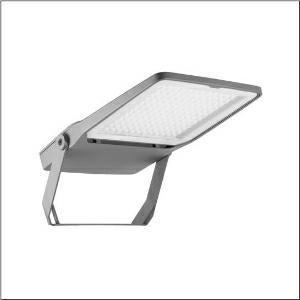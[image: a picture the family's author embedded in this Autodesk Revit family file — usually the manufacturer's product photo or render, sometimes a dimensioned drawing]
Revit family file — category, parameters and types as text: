
# Revit family: floodlight_fl_20_midi___pl52_5xa7681e2d1ac_ecaa
name_source: partatom
category: Lighting Fixtures
units: mm (PartAtom-declared; Revit-internal decimal feet)

## family parameters
Cut with Voids When Loaded = No
Host = Face
Light Source = No
Part Type = Normal
Room Calculation Point = No
Round Connector Dimension = Use Diameter
Shared = No

## types (1)
- Floodlight FL 20 midi  PL52 (1 x LED 4000K / CRI = 70 (unbekannt), 26840 lm, 4000K)
    Apparent Load = 208 VA
    CIE Flux Codes = 27 59 98 100 100
    Color Rendering = 70
    Color Temperature = 4000K
    Default Elevation = 1800 mm
    Description = Floodlight FL 20 midi, floodlight, primary light control with lens, of plastic, primary optical cover: protective disc, of toughened safety glass, transparent, light distribution: PL52, light emission: direct distribution, primary light characteristic: asymmetric, installation type: surface-mounted, LED High Power LED, rated luminous flux: 26.840 lm, light colour: 740, colour temperature: 4000K, control gear: ECG Basic, control: power reduction, overheat protection, electronic power reduction, with terminal, 5-pole, max. 2.5mm², mains connection: 220..240V, AC, 50/60Hz, rated input power: 208W, LED unit, of diecast aluminium, powder-coated, Siteco® metallic grey (DB 702S), length: 654 mm, width: 450 mm, height: 76mm, housing frame, of diecast aluminium, powder-coated, Siteco® metallic grey (DB 702S), mounting bracket, of steel, powder-coated, Siteco® metallic grey (DB 702S), ON/OFFprotection rating (complete): IP66, insulation class (complete): insulation class I (protective earthing), certification: CE, ENEC, VDE, protection symbol: D, permissible ambient temperature for indoor applications: -40..+40°C, permissible ambient temperature for outdoor applications: -40..+50°C, standard: DIN EN 12944, packaging unit: 1 piece

Light Distribution: PL52
    Height = 76 mm
    Lamp = 1 x LED 4000K / CRI >= 70 (unbekannt)
    Lamp Light Flux = 26840 lm
    Lamp count = 1
    Length = 672 mm
    Luminous efficacy = 129 lm/W
    Manufacturer = Siteco
    ModVariant = No
    Model = 5XA7681E2D1AC
    Number of Poles = 1
    OnlyDefault = Yes
    Power Factor = 1
    Product Name = Floodlight FL 20 midi | PL52
    Product group = floodlight | pylon top
    ProductGroupID = 6101
    Protection Class = Protection class I
    Protection Degree = IP 66
    RLX_Detail_Level = 1
    RlxData = <blob elided: 94097 chars, md5=06d9ddb8>
    Socket = socket
    Standby Power = 0 W
    System Light Flux = 26840 lm
    System Power = 208 W
    Type Comments = Product without accessories
    Type Image = l_1005943.jpg
    URL = http://relux.com
    VarID = ---
    Voltage = 0 V
    Weight = 0.00 kg
    Width = 450 mm

## geometry (parser evidence)
native form markers: Blend x4, Sweep x15
no freeform markers — native parametric forms only
